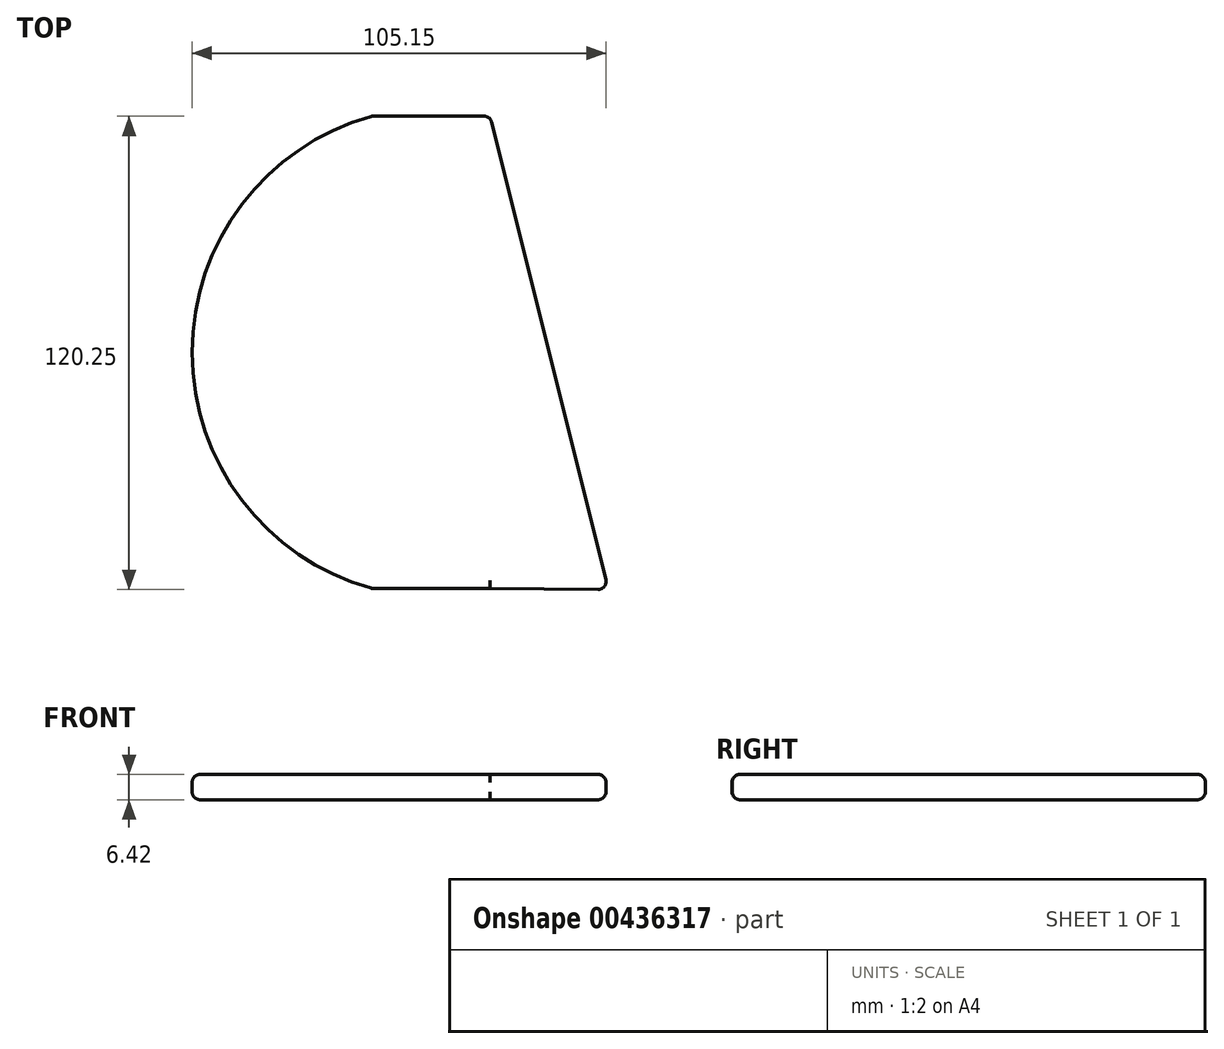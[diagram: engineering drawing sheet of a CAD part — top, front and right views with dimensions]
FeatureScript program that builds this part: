
annotation { "Feature Type Name" : "Feature", "Feature Type Description" : "" }
export const myFeature = defineFeature(function(context is Context, id is Id, definition is map)
    precondition{}
    {
        {
            var Q0;
            Q0=qCreatedBy(makeId("Top.planeOp"),FACE);
            var sketch = newSketch(context, id + "F0", { "sketchPlane" : qUnion([Q0])});
            skLineSegment(sketch, "E0", {"start": v(-17.02, 96.27) * mm, "end": v(12.98, 96.27) * mm});
            skLineSegment(sketch, "E1", {"start": v(12.98, 96.27) * mm, "end": v(12.98, -23.73) * mm});
            skLineSegment(sketch, "E2", {"start": v(12.98, -23.73) * mm, "end": v(-17.02, -23.73) * mm});
            skLineSegment(sketch, "E3", {"start": v(-17.02, -23.73) * mm, "end": v(-17.02, 96.27) * mm});
            skArc(sketch, "E4", {"start": v(-17.02, 96.27) * mm, "mid": v(-62.74, 36.27) * mm, "end": v(-17.02, -23.73) * mm});
            skLineSegment(sketch, "E5", {"start": v(12.98, 96.27) * mm, "end": v(42.98, -24) * mm});
            skLineSegment(sketch, "E6", {"start": v(42.98, -24) * mm, "end": v(12.98, -23.73) * mm});
            skSolve(sketch);
        }
        {
            var Q0;
            Q0=makeQuery(id+"F0.imprint","IMPRINT",FACE,{"disambiguationData":[TD([[makeQuery(id+"F0.imprint","IMPRINT",EDGE,{"derivedFrom":sQuery(id+"F0.wireOp",EDGE,"E3")}),1.0]])]});
            var Q1;
            Q1=makeQuery(id+"F0.imprint","IMPRINT",FACE,{"disambiguationData":[TD([[makeQuery(id+"F0.imprint","IMPRINT",EDGE,{"derivedFrom":sQuery(id+"F0.wireOp",EDGE,"E1")}),1.0]])]});
            var Q2;
            Q2=makeQuery(id+"F0.imprint","IMPRINT",FACE,{"disambiguationData":[TD([[makeQuery(id+"F0.imprint","IMPRINT",EDGE,{"derivedFrom":sQuery(id+"F0.wireOp",EDGE,"E0")}),-1.0]])]});
            extrude(context, id + "F1", {"entities" : qUnion([Q0, Q1, Q2]), "depth" : 6.42 * mm});
        }
        {
            var Q0;
            Q0=makeQuery(id+"F1.opExtrude","SWEPT_FACE",FACE,{"disambiguationData":[OSD([sQuery(id+"F0.wireOp",EDGE,"E4")])]});
            var Q1;
            Q1=makeQuery(id+"F1.opExtrude","SWEPT_FACE",FACE,{"disambiguationData":[OSD([sQuery(id+"F0.wireOp",EDGE,"E0")])]});
            var Q2;
            Q2=makeQuery(id+"F1.opExtrude","SWEPT_FACE",FACE,{"disambiguationData":[OSD([sQuery(id+"F0.wireOp",EDGE,"E5")])]});
            var Q3;
            Q3=makeQuery(id+"F1.opExtrude","CAP_EDGE",EDGE,{"disambiguationData":[OSD([sQuery(id+"F0.wireOp",EDGE,"E2")])],"isStart":true});
            var Q4;
            Q4=makeQuery(id+"F1.opExtrude","CAP_EDGE",EDGE,{"disambiguationData":[OSD([sQuery(id+"F0.wireOp",EDGE,"E6")])],"isStart":true});
            var Q5;
            Q5=makeQuery(id+"F1.opExtrude","CAP_EDGE",EDGE,{"disambiguationData":[OSD([sQuery(id+"F0.wireOp",EDGE,"E2")])],"isStart":false});
            var Q6;
            Q6=makeQuery(id+"F1.opExtrude","CAP_EDGE",EDGE,{"disambiguationData":[OSD([sQuery(id+"F0.wireOp",EDGE,"E6")])],"isStart":false});
            var Q7;
            Q7=makeQuery(id+"F1.opExtrude","CAP_FACE",FACE,{"disambiguationData":[OSD([sQuery(id+"F0.wireOp",EDGE,"E0"),sQuery(id+"F0.wireOp",EDGE,"E2"),sQuery(id+"F0.wireOp",EDGE,"E4"),sQuery(id+"F0.wireOp",EDGE,"E5"),sQuery(id+"F0.wireOp",EDGE,"E6")])],"isStart":false});
            fillet(context, id + "F2", {"entities" : qUnion([Q0, Q1, Q2, Q3, Q4, Q5, Q6, Q7]), "radius" : 2 * mm, "tangentPropagation" : true, "allowEdgeOverflow" : false});
        }
    });
